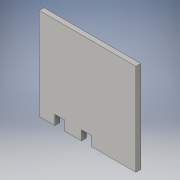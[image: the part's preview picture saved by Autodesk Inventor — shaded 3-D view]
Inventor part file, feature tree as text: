
AUTODESK INVENTOR PART (.ipt)
format: ipt  version: 2016 (Build 200138000, 138)  size: 104,960 bytes
history: native  units: in
note: dims shown in document units (in); Inventor stores cm internally (conversion verified against a paired STEP export)
features: extrude x1, sketch x1
ambient origin geometry x8: Origin, YZ Plane, XZ Plane, XY Plane, X Axis, Y Axis, Z Axis, Center Point
bodies: Solid1 (feature_tree)
feature tree (2):
  extrude  "Extrusion1"  Depth=9.5in
  sketch  "Sketch1"  dims[d0=10.0in d1=9.5in d2=3.5in d3=1.0in d4=1.0in d5=1.0in d6=0.875in d7=0.875in d8=0.5in d9=0.0in]
